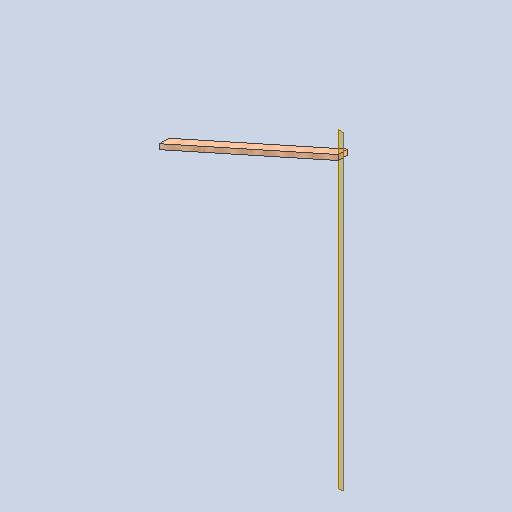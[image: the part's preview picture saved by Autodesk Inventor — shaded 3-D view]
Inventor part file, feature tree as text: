
AUTODESK INVENTOR PART (.ipt)
format: ipt  version: 2025 (Build 290162000, 162)  size: 145,408 bytes
history: native  units: in
note: dims shown in document units (in); Inventor stores cm internally (conversion verified against a paired STEP export)
features: other x5, reference x3, plane x2, extrude x1, sketch x1
ambient origin geometry x8: Origin, YZ Plane, XZ Plane, XY Plane, X Axis, Y Axis, Z Axis, Center Point
bodies: Body1 (feature_tree)
feature tree (12):
  plane  "Work Plane1"
  plane  "Work Plane2"
  extrude  "Extrusion2"  Depth=4.0in TaperAngle=0.0deg
  sketch  "Sketch2"  dims[d1=2.0in d4=4.0in d5=0.0in]
  reference  "Reference3"
  reference  "Reference4"
  reference  "Reference5"
  other  "<userpath>\Documents\GitHub\USCTigerBurn24\v2\Tiger.iam"
  other  "Tiger.iam"
  other  "2x4x48:11"
  other  "2x4x72:7"
  other  "2x4x120:6"
